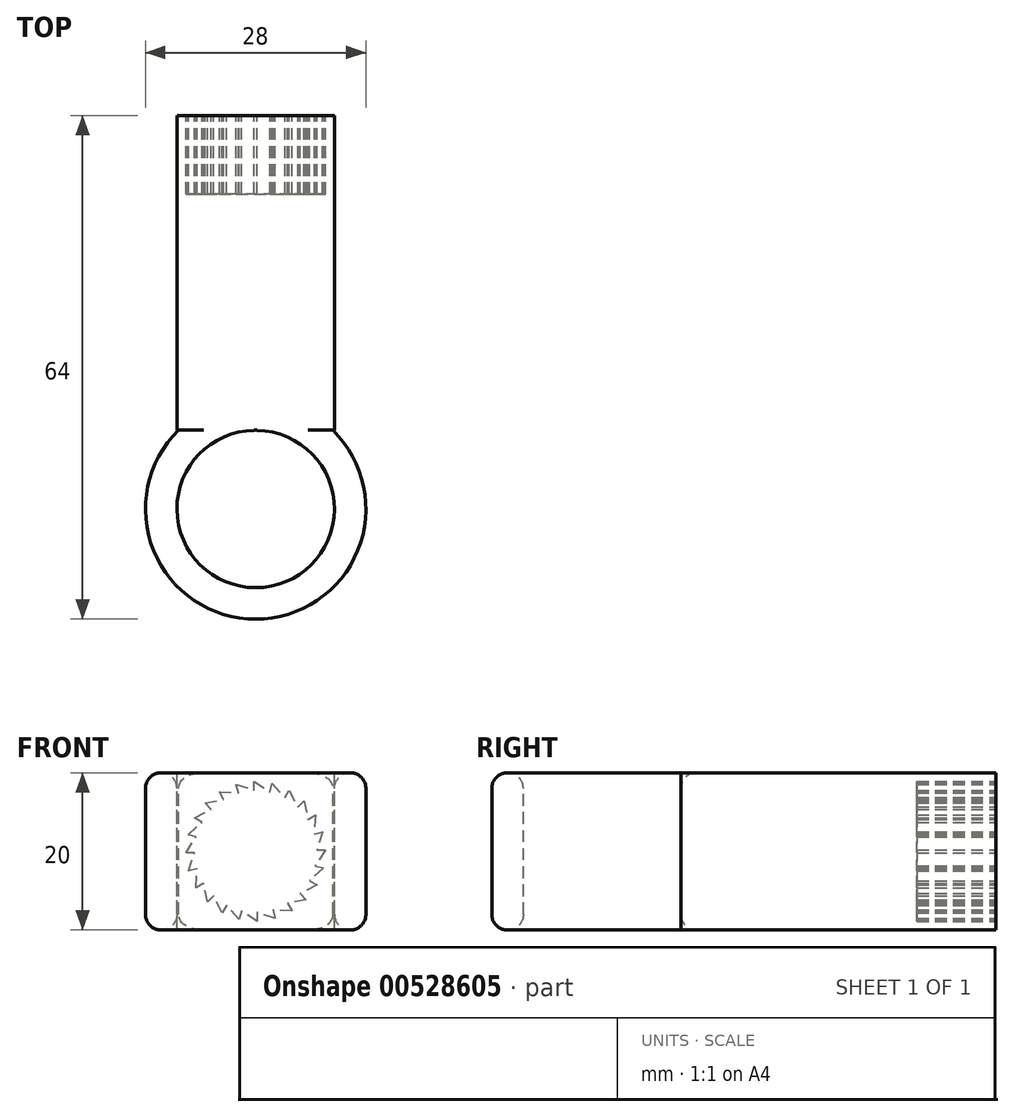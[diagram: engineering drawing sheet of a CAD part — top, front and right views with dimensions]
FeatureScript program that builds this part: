
annotation { "Feature Type Name" : "Feature", "Feature Type Description" : "" }
export const myFeature = defineFeature(function(context is Context, id is Id, definition is map)
    precondition{}
    {
        {
            var Q0;
            Q0=qCreatedBy(makeId("Front.planeOp"),FACE);
            var sketch = newSketch(context, id + "F0", { "sketchPlane" : qUnion([Q0])});
            skLineSegment(sketch, "E0.bottom", {"start": v(0, 0) * mm, "end": v(20, 0) * mm});
            skLineSegment(sketch, "E0.top", {"start": v(0, 20) * mm, "end": v(20, 20) * mm});
            skLineSegment(sketch, "E0.left", {"start": v(0, 0) * mm, "end": v(0, 20) * mm});
            skLineSegment(sketch, "E0.right", {"start": v(20, 0) * mm, "end": v(20, 20) * mm});
            skCircle(sketch, "E1", {"center": v(10, 10) * mm, "radius": 7.5 * mm});
            skLineSegment(sketch, "E2", {"start": v(10, 17.5) * mm, "end": v(10, 18.5) * mm});
            skPoint(sketch, "E3.center", {"position": v(13.24, 8.82) * mm});
            skLineSegment(sketch, "E4", {"start": v(10, 18.5) * mm, "end": v(11.94, 17.24) * mm});
            skLineSegment(sketch, "E5.1.0", {"start": v(12.2, 18.21) * mm, "end": v(13.75, 16.5) * mm});
            skLineSegment(sketch, "E5.1.1", {"start": v(11.94, 17.24) * mm, "end": v(12.2, 18.21) * mm});
            skLineSegment(sketch, "E5.2.0", {"start": v(14.25, 17.36) * mm, "end": v(15.3, 15.3) * mm});
            skLineSegment(sketch, "E5.2.1", {"start": v(13.75, 16.5) * mm, "end": v(14.25, 17.36) * mm});
            skLineSegment(sketch, "E5.3.0", {"start": v(16.01, 16.01) * mm, "end": v(16.5, 13.75) * mm});
            skLineSegment(sketch, "E5.3.1", {"start": v(15.3, 15.3) * mm, "end": v(16.01, 16.01) * mm});
            skLineSegment(sketch, "E5.4.0", {"start": v(17.36, 14.25) * mm, "end": v(17.24, 11.94) * mm});
            skLineSegment(sketch, "E5.4.1", {"start": v(16.5, 13.75) * mm, "end": v(17.36, 14.25) * mm});
            skLineSegment(sketch, "E5.5.0", {"start": v(18.21, 12.2) * mm, "end": v(17.5, 10) * mm});
            skLineSegment(sketch, "E5.5.1", {"start": v(17.24, 11.94) * mm, "end": v(18.21, 12.2) * mm});
            skLineSegment(sketch, "E5.6.0", {"start": v(18.5, 10) * mm, "end": v(17.24, 8.06) * mm});
            skLineSegment(sketch, "E5.6.1", {"start": v(17.5, 10) * mm, "end": v(18.5, 10) * mm});
            skLineSegment(sketch, "E5.7.0", {"start": v(18.21, 7.8) * mm, "end": v(16.5, 6.25) * mm});
            skLineSegment(sketch, "E5.7.1", {"start": v(17.24, 8.06) * mm, "end": v(18.21, 7.8) * mm});
            skLineSegment(sketch, "E5.8.0", {"start": v(17.36, 5.75) * mm, "end": v(15.3, 4.7) * mm});
            skLineSegment(sketch, "E5.8.1", {"start": v(16.5, 6.25) * mm, "end": v(17.36, 5.75) * mm});
            skLineSegment(sketch, "E5.9.0", {"start": v(16.01, 3.99) * mm, "end": v(13.75, 3.5) * mm});
            skLineSegment(sketch, "E5.9.1", {"start": v(15.3, 4.7) * mm, "end": v(16.01, 3.99) * mm});
            skLineSegment(sketch, "E5.10.0", {"start": v(14.25, 2.64) * mm, "end": v(11.94, 2.76) * mm});
            skLineSegment(sketch, "E5.10.1", {"start": v(13.75, 3.5) * mm, "end": v(14.25, 2.64) * mm});
            skLineSegment(sketch, "E5.11.0", {"start": v(12.2, 1.79) * mm, "end": v(10, 2.5) * mm});
            skLineSegment(sketch, "E5.11.1", {"start": v(11.94, 2.76) * mm, "end": v(12.2, 1.79) * mm});
            skLineSegment(sketch, "E5.12.0", {"start": v(10, 1.5) * mm, "end": v(8.06, 2.76) * mm});
            skLineSegment(sketch, "E5.12.1", {"start": v(10, 2.5) * mm, "end": v(10, 1.5) * mm});
            skLineSegment(sketch, "E5.13.0", {"start": v(7.8, 1.79) * mm, "end": v(6.25, 3.5) * mm});
            skLineSegment(sketch, "E5.13.1", {"start": v(8.06, 2.76) * mm, "end": v(7.8, 1.79) * mm});
            skLineSegment(sketch, "E5.14.0", {"start": v(5.75, 2.64) * mm, "end": v(4.7, 4.7) * mm});
            skLineSegment(sketch, "E5.14.1", {"start": v(6.25, 3.5) * mm, "end": v(5.75, 2.64) * mm});
            skLineSegment(sketch, "E5.15.0", {"start": v(3.99, 3.99) * mm, "end": v(3.5, 6.25) * mm});
            skLineSegment(sketch, "E5.15.1", {"start": v(4.7, 4.7) * mm, "end": v(3.99, 3.99) * mm});
            skLineSegment(sketch, "E5.16.0", {"start": v(2.64, 5.75) * mm, "end": v(2.76, 8.06) * mm});
            skLineSegment(sketch, "E5.16.1", {"start": v(3.5, 6.25) * mm, "end": v(2.64, 5.75) * mm});
            skLineSegment(sketch, "E5.17.0", {"start": v(1.79, 7.8) * mm, "end": v(2.5, 10) * mm});
            skLineSegment(sketch, "E5.17.1", {"start": v(2.76, 8.06) * mm, "end": v(1.79, 7.8) * mm});
            skLineSegment(sketch, "E5.18.0", {"start": v(1.5, 10) * mm, "end": v(2.76, 11.94) * mm});
            skLineSegment(sketch, "E5.18.1", {"start": v(2.5, 10) * mm, "end": v(1.5, 10) * mm});
            skLineSegment(sketch, "E5.19.0", {"start": v(1.79, 12.2) * mm, "end": v(3.5, 13.75) * mm});
            skLineSegment(sketch, "E5.19.1", {"start": v(2.76, 11.94) * mm, "end": v(1.79, 12.2) * mm});
            skLineSegment(sketch, "E5.20.0", {"start": v(2.64, 14.25) * mm, "end": v(4.7, 15.3) * mm});
            skLineSegment(sketch, "E5.20.1", {"start": v(3.5, 13.75) * mm, "end": v(2.64, 14.25) * mm});
            skLineSegment(sketch, "E5.21.0", {"start": v(3.99, 16.01) * mm, "end": v(6.25, 16.5) * mm});
            skLineSegment(sketch, "E5.21.1", {"start": v(4.7, 15.3) * mm, "end": v(3.99, 16.01) * mm});
            skLineSegment(sketch, "E5.22.0", {"start": v(5.75, 17.36) * mm, "end": v(8.06, 17.24) * mm});
            skLineSegment(sketch, "E5.22.1", {"start": v(6.25, 16.5) * mm, "end": v(5.75, 17.36) * mm});
            skLineSegment(sketch, "E5.anchor1", {"start": v(10, 10) * mm, "end": v(10, 17.5) * mm, "construction": true});
            skLineSegment(sketch, "E5.anchor2", {"start": v(10, 10) * mm, "end": v(8.06, 17.24) * mm, "construction": true});
            skLineSegment(sketch, "E6.3.23.0", {"start": v(8.06, 17.24) * mm, "end": v(7.8, 18.21) * mm});
            skLineSegment(sketch, "E6.4.23.0", {"start": v(7.8, 18.21) * mm, "end": v(10, 17.5) * mm});
            skLineSegment(sketch, "E7.0", {"start": v(18.51, 12.49) * mm, "end": v(17.77, 10.2) * mm});
            skLineSegment(sketch, "E7.1", {"start": v(17.46, 12.2) * mm, "end": v(18.51, 12.49) * mm});
            skLineSegment(sketch, "E7.2", {"start": v(2.42, 5.4) * mm, "end": v(2.54, 7.8) * mm});
            skLineSegment(sketch, "E7.3", {"start": v(3.37, 5.94) * mm, "end": v(2.42, 5.4) * mm});
            skLineSegment(sketch, "E7.4", {"start": v(3.87, 3.59) * mm, "end": v(3.37, 5.94) * mm});
            skLineSegment(sketch, "E7.5", {"start": v(4.64, 4.36) * mm, "end": v(3.87, 3.59) * mm});
            skLineSegment(sketch, "E7.6", {"start": v(5.74, 2.22) * mm, "end": v(4.64, 4.36) * mm});
            skLineSegment(sketch, "E7.7", {"start": v(6.29, 3.17) * mm, "end": v(5.74, 2.22) * mm});
            skLineSegment(sketch, "E7.8", {"start": v(7.9, 1.38) * mm, "end": v(6.29, 3.17) * mm});
            skLineSegment(sketch, "E7.9", {"start": v(8.18, 2.44) * mm, "end": v(7.9, 1.38) * mm});
            skLineSegment(sketch, "E7.10", {"start": v(10.2, 1.13) * mm, "end": v(8.18, 2.44) * mm});
            skLineSegment(sketch, "E7.11", {"start": v(10.2, 2.23) * mm, "end": v(10.2, 1.13) * mm});
            skLineSegment(sketch, "E7.12", {"start": v(12.49, 1.49) * mm, "end": v(10.2, 2.23) * mm});
            skLineSegment(sketch, "E7.13", {"start": v(12.2, 2.54) * mm, "end": v(12.49, 1.49) * mm});
            skLineSegment(sketch, "E7.14", {"start": v(18.62, 7.9) * mm, "end": v(16.83, 6.29) * mm});
            skLineSegment(sketch, "E7.15", {"start": v(17.56, 8.18) * mm, "end": v(18.62, 7.9) * mm});
            skLineSegment(sketch, "E7.16", {"start": v(18.87, 10.2) * mm, "end": v(17.56, 8.18) * mm});
            skLineSegment(sketch, "E7.17", {"start": v(17.77, 10.2) * mm, "end": v(18.87, 10.2) * mm});
            skLineSegment(sketch, "E7.18", {"start": v(16.83, 6.29) * mm, "end": v(17.78, 5.74) * mm});
            skLineSegment(sketch, "E7.19", {"start": v(17.78, 5.74) * mm, "end": v(15.64, 4.64) * mm});
            skLineSegment(sketch, "E7.20", {"start": v(15.64, 4.64) * mm, "end": v(16.41, 3.87) * mm});
            skLineSegment(sketch, "E7.21", {"start": v(16.41, 3.87) * mm, "end": v(14.06, 3.37) * mm});
            skLineSegment(sketch, "E7.22", {"start": v(14.06, 3.37) * mm, "end": v(14.6, 2.42) * mm});
            skLineSegment(sketch, "E7.23", {"start": v(14.6, 2.42) * mm, "end": v(12.2, 2.54) * mm});
            skLineSegment(sketch, "E7.24", {"start": v(2.54, 7.8) * mm, "end": v(1.49, 7.51) * mm});
            skLineSegment(sketch, "E7.25", {"start": v(1.49, 7.51) * mm, "end": v(2.23, 9.8) * mm});
            skLineSegment(sketch, "E7.26", {"start": v(2.23, 9.8) * mm, "end": v(1.13, 9.8) * mm});
            skLineSegment(sketch, "E7.27", {"start": v(1.13, 9.8) * mm, "end": v(2.44, 11.82) * mm});
            skLineSegment(sketch, "E7.28", {"start": v(2.44, 11.82) * mm, "end": v(1.38, 12.1) * mm});
            skLineSegment(sketch, "E7.29", {"start": v(1.38, 12.1) * mm, "end": v(3.17, 13.71) * mm});
            skLineSegment(sketch, "E7.30", {"start": v(3.17, 13.71) * mm, "end": v(2.22, 14.26) * mm});
            skLineSegment(sketch, "E7.31", {"start": v(2.22, 14.26) * mm, "end": v(4.36, 15.36) * mm});
            skLineSegment(sketch, "E7.32", {"start": v(4.36, 15.36) * mm, "end": v(3.59, 16.13) * mm});
            skLineSegment(sketch, "E7.33", {"start": v(3.59, 16.13) * mm, "end": v(5.94, 16.63) * mm});
            skLineSegment(sketch, "E7.34", {"start": v(5.94, 16.63) * mm, "end": v(5.4, 17.58) * mm});
            skLineSegment(sketch, "E7.35", {"start": v(5.4, 17.58) * mm, "end": v(7.8, 17.46) * mm});
            skLineSegment(sketch, "E7.36", {"start": v(7.8, 17.46) * mm, "end": v(7.51, 18.51) * mm});
            skLineSegment(sketch, "E7.37", {"start": v(7.51, 18.51) * mm, "end": v(9.8, 17.77) * mm});
            skLineSegment(sketch, "E7.38", {"start": v(9.8, 17.77) * mm, "end": v(9.8, 18.87) * mm});
            skLineSegment(sketch, "E7.39", {"start": v(9.8, 18.87) * mm, "end": v(11.82, 17.56) * mm});
            skLineSegment(sketch, "E7.40", {"start": v(11.82, 17.56) * mm, "end": v(12.1, 18.62) * mm});
            skLineSegment(sketch, "E7.41", {"start": v(12.1, 18.62) * mm, "end": v(13.71, 16.83) * mm});
            skLineSegment(sketch, "E7.42", {"start": v(13.71, 16.83) * mm, "end": v(14.26, 17.78) * mm});
            skLineSegment(sketch, "E7.43", {"start": v(14.26, 17.78) * mm, "end": v(15.36, 15.64) * mm});
            skLineSegment(sketch, "E7.44", {"start": v(15.36, 15.64) * mm, "end": v(16.13, 16.41) * mm});
            skLineSegment(sketch, "E7.45", {"start": v(16.13, 16.41) * mm, "end": v(16.63, 14.06) * mm});
            skLineSegment(sketch, "E7.46", {"start": v(16.63, 14.06) * mm, "end": v(17.58, 14.6) * mm});
            skLineSegment(sketch, "E7.47", {"start": v(17.58, 14.6) * mm, "end": v(17.46, 12.2) * mm});
            skSolve(sketch);
        }
        {
            var Q0;
            Q0 = qSketchRegion(id + "F0", true);
            var Q1;
            {var subQ0=sQuery(id+"F0.wireOp",EDGE,"E1");var subQ17=makeQuery(id+"F0.imprint","INTERSECT",VERTEX,{"derivedFrom":[subQ0,sQuery(id+"F0.wireOp",EDGE,"E5.4.0"),sQuery(id+"F0.wireOp",EDGE,"E5.5.1")]});Q1=makeQuery(id+"F0.imprint","IMPRINT",FACE,{"disambiguationData":[TD([[makeQuery(id+"F0.imprint","IMPRINT",EDGE,{"disambiguationData":[TD([[subQ17,1.0]])],"derivedFrom":subQ0}),1.0]])]});}
            var Q2;
            {var subQ2=sQuery(id+"F0.wireOp",EDGE,"E5.19.0");Q2=makeQuery(id+"F0.imprint","IMPRINT",FACE,{"disambiguationData":[TD([[makeQuery(id+"F0.imprint","IMPRINT",EDGE,{"derivedFrom":subQ2}),-1.0]])]});}
            var Q3;
            {var subQ2=sQuery(id+"F0.wireOp",EDGE,"E5.20.0");Q3=makeQuery(id+"F0.imprint","IMPRINT",FACE,{"disambiguationData":[TD([[makeQuery(id+"F0.imprint","IMPRINT",EDGE,{"derivedFrom":subQ2}),-1.0]])]});}
            var Q4;
            {var subQ2=sQuery(id+"F0.wireOp",EDGE,"E5.21.0");Q4=makeQuery(id+"F0.imprint","IMPRINT",FACE,{"disambiguationData":[TD([[makeQuery(id+"F0.imprint","IMPRINT",EDGE,{"derivedFrom":subQ2}),-1.0]])]});}
            var Q5;
            Q5=makeQuery(id+"F0.imprint","IMPRINT",FACE,{"disambiguationData":[TD([[makeQuery(id+"F0.imprint","IMPRINT",EDGE,{"derivedFrom":sQuery(id+"F0.wireOp",EDGE,"E2")}),1.0]])]});
            var Q6;
            {var subQ2=sQuery(id+"F0.wireOp",EDGE,"E5.22.0");Q6=makeQuery(id+"F0.imprint","IMPRINT",FACE,{"disambiguationData":[TD([[makeQuery(id+"F0.imprint","IMPRINT",EDGE,{"derivedFrom":subQ2}),-1.0]])]});}
            var Q7;
            {var subQ2=sQuery(id+"F0.wireOp",EDGE,"E6.3.23.0");Q7=makeQuery(id+"F0.imprint","IMPRINT",FACE,{"disambiguationData":[TD([[makeQuery(id+"F0.imprint","IMPRINT",EDGE,{"derivedFrom":subQ2}),-1.0]])]});}
            var Q8;
            {var subQ0=sQuery(id+"F0.wireOp",EDGE,"E2");Q8=makeQuery(id+"F0.imprint","IMPRINT",FACE,{"disambiguationData":[TD([[makeQuery(id+"F0.imprint","IMPRINT",EDGE,{"derivedFrom":subQ0}),-1.0]])]});}
            var Q9;
            {var subQ2=sQuery(id+"F0.wireOp",EDGE,"E5.1.0");Q9=makeQuery(id+"F0.imprint","IMPRINT",FACE,{"disambiguationData":[TD([[makeQuery(id+"F0.imprint","IMPRINT",EDGE,{"derivedFrom":subQ2}),-1.0]])]});}
            var Q10;
            {var subQ2=sQuery(id+"F0.wireOp",EDGE,"E5.2.0");Q10=makeQuery(id+"F0.imprint","IMPRINT",FACE,{"disambiguationData":[TD([[makeQuery(id+"F0.imprint","IMPRINT",EDGE,{"derivedFrom":subQ2}),-1.0]])]});}
            var Q11;
            {var subQ2=sQuery(id+"F0.wireOp",EDGE,"E5.3.0");Q11=makeQuery(id+"F0.imprint","IMPRINT",FACE,{"disambiguationData":[TD([[makeQuery(id+"F0.imprint","IMPRINT",EDGE,{"derivedFrom":subQ2}),-1.0]])]});}
            var Q12;
            {var subQ2=sQuery(id+"F0.wireOp",EDGE,"E5.4.0");Q12=makeQuery(id+"F0.imprint","IMPRINT",FACE,{"disambiguationData":[TD([[makeQuery(id+"F0.imprint","IMPRINT",EDGE,{"derivedFrom":subQ2}),-1.0]])]});}
            var Q13;
            {var subQ2=sQuery(id+"F0.wireOp",EDGE,"E5.5.0");Q13=makeQuery(id+"F0.imprint","IMPRINT",FACE,{"disambiguationData":[TD([[makeQuery(id+"F0.imprint","IMPRINT",EDGE,{"derivedFrom":subQ2}),-1.0]])]});}
            var Q14;
            {var subQ2=sQuery(id+"F0.wireOp",EDGE,"E5.6.0");Q14=makeQuery(id+"F0.imprint","IMPRINT",FACE,{"disambiguationData":[TD([[makeQuery(id+"F0.imprint","IMPRINT",EDGE,{"derivedFrom":subQ2}),-1.0]])]});}
            var Q15;
            {var subQ2=sQuery(id+"F0.wireOp",EDGE,"E5.7.0");Q15=makeQuery(id+"F0.imprint","IMPRINT",FACE,{"disambiguationData":[TD([[makeQuery(id+"F0.imprint","IMPRINT",EDGE,{"derivedFrom":subQ2}),-1.0]])]});}
            var Q16;
            {var subQ2=sQuery(id+"F0.wireOp",EDGE,"E5.8.0");Q16=makeQuery(id+"F0.imprint","IMPRINT",FACE,{"disambiguationData":[TD([[makeQuery(id+"F0.imprint","IMPRINT",EDGE,{"derivedFrom":subQ2}),-1.0]])]});}
            var Q17;
            {var subQ2=sQuery(id+"F0.wireOp",EDGE,"E5.9.0");Q17=makeQuery(id+"F0.imprint","IMPRINT",FACE,{"disambiguationData":[TD([[makeQuery(id+"F0.imprint","IMPRINT",EDGE,{"derivedFrom":subQ2}),-1.0]])]});}
            var Q18;
            {var subQ2=sQuery(id+"F0.wireOp",EDGE,"E5.10.0");Q18=makeQuery(id+"F0.imprint","IMPRINT",FACE,{"disambiguationData":[TD([[makeQuery(id+"F0.imprint","IMPRINT",EDGE,{"derivedFrom":subQ2}),-1.0]])]});}
            var Q19;
            {var subQ2=sQuery(id+"F0.wireOp",EDGE,"E5.11.0");Q19=makeQuery(id+"F0.imprint","IMPRINT",FACE,{"disambiguationData":[TD([[makeQuery(id+"F0.imprint","IMPRINT",EDGE,{"derivedFrom":subQ2}),-1.0]])]});}
            var Q20;
            {var subQ2=sQuery(id+"F0.wireOp",EDGE,"E5.12.0");Q20=makeQuery(id+"F0.imprint","IMPRINT",FACE,{"disambiguationData":[TD([[makeQuery(id+"F0.imprint","IMPRINT",EDGE,{"derivedFrom":subQ2}),-1.0]])]});}
            var Q21;
            {var subQ2=sQuery(id+"F0.wireOp",EDGE,"E5.13.0");Q21=makeQuery(id+"F0.imprint","IMPRINT",FACE,{"disambiguationData":[TD([[makeQuery(id+"F0.imprint","IMPRINT",EDGE,{"derivedFrom":subQ2}),-1.0]])]});}
            var Q22;
            {var subQ2=sQuery(id+"F0.wireOp",EDGE,"E5.14.0");Q22=makeQuery(id+"F0.imprint","IMPRINT",FACE,{"disambiguationData":[TD([[makeQuery(id+"F0.imprint","IMPRINT",EDGE,{"derivedFrom":subQ2}),-1.0]])]});}
            var Q23;
            {var subQ2=sQuery(id+"F0.wireOp",EDGE,"E5.15.0");Q23=makeQuery(id+"F0.imprint","IMPRINT",FACE,{"disambiguationData":[TD([[makeQuery(id+"F0.imprint","IMPRINT",EDGE,{"derivedFrom":subQ2}),-1.0]])]});}
            var Q24;
            {var subQ2=sQuery(id+"F0.wireOp",EDGE,"E5.16.0");Q24=makeQuery(id+"F0.imprint","IMPRINT",FACE,{"disambiguationData":[TD([[makeQuery(id+"F0.imprint","IMPRINT",EDGE,{"derivedFrom":subQ2}),-1.0]])]});}
            var Q25;
            {var subQ2=sQuery(id+"F0.wireOp",EDGE,"E5.17.0");Q25=makeQuery(id+"F0.imprint","IMPRINT",FACE,{"disambiguationData":[TD([[makeQuery(id+"F0.imprint","IMPRINT",EDGE,{"derivedFrom":subQ2}),-1.0]])]});}
            var Q26;
            {var subQ2=sQuery(id+"F0.wireOp",EDGE,"E5.18.0");Q26=makeQuery(id+"F0.imprint","IMPRINT",FACE,{"disambiguationData":[TD([[makeQuery(id+"F0.imprint","IMPRINT",EDGE,{"derivedFrom":subQ2}),-1.0]])]});}
            extrude(context, id + "F1", {"entities" : qUnion([Q0, Q1, Q2, Q3, Q4, Q5, Q6, Q7, Q8, Q9, Q10, Q11, Q12, Q13, Q14, Q15, Q16, Q17, Q18, Q19, Q20, Q21, Q22, Q23, Q24, Q25, Q26]), "depth" : 40 * mm, "offsetDistance" : 25 * mm});
        }
        {
            var Q0;
            {var subQ0=sQuery(id+"F0.wireOp",EDGE,"E1");var subQ17=makeQuery(id+"F0.imprint","INTERSECT",VERTEX,{"derivedFrom":[subQ0,sQuery(id+"F0.wireOp",EDGE,"E5.4.0"),sQuery(id+"F0.wireOp",EDGE,"E5.5.1")]});Q0=makeQuery(id+"F0.imprint","IMPRINT",FACE,{"disambiguationData":[TD([[makeQuery(id+"F0.imprint","IMPRINT",EDGE,{"disambiguationData":[TD([[subQ17,1.0]])],"derivedFrom":subQ0}),1.0]])]});}
            var Q1;
            {var subQ2=sQuery(id+"F0.wireOp",EDGE,"E5.3.0");Q1=makeQuery(id+"F0.imprint","IMPRINT",FACE,{"disambiguationData":[TD([[makeQuery(id+"F0.imprint","IMPRINT",EDGE,{"derivedFrom":subQ2}),-1.0]])]});}
            var Q2;
            {var subQ2=sQuery(id+"F0.wireOp",EDGE,"E5.2.0");Q2=makeQuery(id+"F0.imprint","IMPRINT",FACE,{"disambiguationData":[TD([[makeQuery(id+"F0.imprint","IMPRINT",EDGE,{"derivedFrom":subQ2}),-1.0]])]});}
            var Q3;
            {var subQ2=sQuery(id+"F0.wireOp",EDGE,"E5.1.0");Q3=makeQuery(id+"F0.imprint","IMPRINT",FACE,{"disambiguationData":[TD([[makeQuery(id+"F0.imprint","IMPRINT",EDGE,{"derivedFrom":subQ2}),-1.0]])]});}
            var Q4;
            {var subQ0=sQuery(id+"F0.wireOp",EDGE,"E2");Q4=makeQuery(id+"F0.imprint","IMPRINT",FACE,{"disambiguationData":[TD([[makeQuery(id+"F0.imprint","IMPRINT",EDGE,{"derivedFrom":subQ0}),-1.0]])]});}
            var Q5;
            {var subQ2=sQuery(id+"F0.wireOp",EDGE,"E6.3.23.0");Q5=makeQuery(id+"F0.imprint","IMPRINT",FACE,{"disambiguationData":[TD([[makeQuery(id+"F0.imprint","IMPRINT",EDGE,{"derivedFrom":subQ2}),-1.0]])]});}
            var Q6;
            {var subQ2=sQuery(id+"F0.wireOp",EDGE,"E5.22.0");Q6=makeQuery(id+"F0.imprint","IMPRINT",FACE,{"disambiguationData":[TD([[makeQuery(id+"F0.imprint","IMPRINT",EDGE,{"derivedFrom":subQ2}),-1.0]])]});}
            var Q7;
            {var subQ2=sQuery(id+"F0.wireOp",EDGE,"E5.21.0");Q7=makeQuery(id+"F0.imprint","IMPRINT",FACE,{"disambiguationData":[TD([[makeQuery(id+"F0.imprint","IMPRINT",EDGE,{"derivedFrom":subQ2}),-1.0]])]});}
            var Q8;
            {var subQ2=sQuery(id+"F0.wireOp",EDGE,"E5.20.0");Q8=makeQuery(id+"F0.imprint","IMPRINT",FACE,{"disambiguationData":[TD([[makeQuery(id+"F0.imprint","IMPRINT",EDGE,{"derivedFrom":subQ2}),-1.0]])]});}
            var Q9;
            {var subQ2=sQuery(id+"F0.wireOp",EDGE,"E5.19.0");Q9=makeQuery(id+"F0.imprint","IMPRINT",FACE,{"disambiguationData":[TD([[makeQuery(id+"F0.imprint","IMPRINT",EDGE,{"derivedFrom":subQ2}),-1.0]])]});}
            var Q10;
            {var subQ2=sQuery(id+"F0.wireOp",EDGE,"E5.18.0");Q10=makeQuery(id+"F0.imprint","IMPRINT",FACE,{"disambiguationData":[TD([[makeQuery(id+"F0.imprint","IMPRINT",EDGE,{"derivedFrom":subQ2}),-1.0]])]});}
            var Q11;
            {var subQ2=sQuery(id+"F0.wireOp",EDGE,"E5.17.0");Q11=makeQuery(id+"F0.imprint","IMPRINT",FACE,{"disambiguationData":[TD([[makeQuery(id+"F0.imprint","IMPRINT",EDGE,{"derivedFrom":subQ2}),-1.0]])]});}
            var Q12;
            {var subQ2=sQuery(id+"F0.wireOp",EDGE,"E5.16.0");Q12=makeQuery(id+"F0.imprint","IMPRINT",FACE,{"disambiguationData":[TD([[makeQuery(id+"F0.imprint","IMPRINT",EDGE,{"derivedFrom":subQ2}),-1.0]])]});}
            var Q13;
            {var subQ2=sQuery(id+"F0.wireOp",EDGE,"E5.15.0");Q13=makeQuery(id+"F0.imprint","IMPRINT",FACE,{"disambiguationData":[TD([[makeQuery(id+"F0.imprint","IMPRINT",EDGE,{"derivedFrom":subQ2}),-1.0]])]});}
            var Q14;
            {var subQ2=sQuery(id+"F0.wireOp",EDGE,"E5.14.0");Q14=makeQuery(id+"F0.imprint","IMPRINT",FACE,{"disambiguationData":[TD([[makeQuery(id+"F0.imprint","IMPRINT",EDGE,{"derivedFrom":subQ2}),-1.0]])]});}
            var Q15;
            {var subQ2=sQuery(id+"F0.wireOp",EDGE,"E5.13.0");Q15=makeQuery(id+"F0.imprint","IMPRINT",FACE,{"disambiguationData":[TD([[makeQuery(id+"F0.imprint","IMPRINT",EDGE,{"derivedFrom":subQ2}),-1.0]])]});}
            var Q16;
            {var subQ2=sQuery(id+"F0.wireOp",EDGE,"E5.12.0");Q16=makeQuery(id+"F0.imprint","IMPRINT",FACE,{"disambiguationData":[TD([[makeQuery(id+"F0.imprint","IMPRINT",EDGE,{"derivedFrom":subQ2}),-1.0]])]});}
            var Q17;
            {var subQ2=sQuery(id+"F0.wireOp",EDGE,"E5.11.0");Q17=makeQuery(id+"F0.imprint","IMPRINT",FACE,{"disambiguationData":[TD([[makeQuery(id+"F0.imprint","IMPRINT",EDGE,{"derivedFrom":subQ2}),-1.0]])]});}
            var Q18;
            {var subQ2=sQuery(id+"F0.wireOp",EDGE,"E5.10.0");Q18=makeQuery(id+"F0.imprint","IMPRINT",FACE,{"disambiguationData":[TD([[makeQuery(id+"F0.imprint","IMPRINT",EDGE,{"derivedFrom":subQ2}),-1.0]])]});}
            var Q19;
            {var subQ2=sQuery(id+"F0.wireOp",EDGE,"E5.9.0");Q19=makeQuery(id+"F0.imprint","IMPRINT",FACE,{"disambiguationData":[TD([[makeQuery(id+"F0.imprint","IMPRINT",EDGE,{"derivedFrom":subQ2}),-1.0]])]});}
            var Q20;
            {var subQ2=sQuery(id+"F0.wireOp",EDGE,"E5.6.0");Q20=makeQuery(id+"F0.imprint","IMPRINT",FACE,{"disambiguationData":[TD([[makeQuery(id+"F0.imprint","IMPRINT",EDGE,{"derivedFrom":subQ2}),-1.0]])]});}
            var Q21;
            {var subQ2=sQuery(id+"F0.wireOp",EDGE,"E5.7.0");Q21=makeQuery(id+"F0.imprint","IMPRINT",FACE,{"disambiguationData":[TD([[makeQuery(id+"F0.imprint","IMPRINT",EDGE,{"derivedFrom":subQ2}),-1.0]])]});}
            var Q22;
            {var subQ2=sQuery(id+"F0.wireOp",EDGE,"E5.8.0");Q22=makeQuery(id+"F0.imprint","IMPRINT",FACE,{"disambiguationData":[TD([[makeQuery(id+"F0.imprint","IMPRINT",EDGE,{"derivedFrom":subQ2}),-1.0]])]});}
            var Q23;
            {var subQ2=sQuery(id+"F0.wireOp",EDGE,"E5.5.0");Q23=makeQuery(id+"F0.imprint","IMPRINT",FACE,{"disambiguationData":[TD([[makeQuery(id+"F0.imprint","IMPRINT",EDGE,{"derivedFrom":subQ2}),-1.0]])]});}
            var Q24;
            {var subQ2=sQuery(id+"F0.wireOp",EDGE,"E5.4.0");Q24=makeQuery(id+"F0.imprint","IMPRINT",FACE,{"disambiguationData":[TD([[makeQuery(id+"F0.imprint","IMPRINT",EDGE,{"derivedFrom":subQ2}),-1.0]])]});}
            var Q25;
            Q25=makeQuery(id+"F0.imprint","IMPRINT",FACE,{"disambiguationData":[TD([[makeQuery(id+"F0.imprint","IMPRINT",EDGE,{"derivedFrom":sQuery(id+"F0.wireOp",EDGE,"E2")}),1.0]])]});
            extrude(context, id + "F2", {"entities" : qUnion([Q0, Q1, Q2, Q3, Q4, Q5, Q6, Q7, Q8, Q9, Q10, Q11, Q12, Q13, Q14, Q15, Q16, Q17, Q18, Q19, Q20, Q21, Q22, Q23, Q24, Q25]), "operationType" : NewBodyOperationType.REMOVE, "depth" : 10 * mm, "offsetDistance" : 25 * mm});
        }
        {
            var Q0;
            Q0=makeQuery(id+"F1.opExtrude","SWEPT_FACE",FACE,{"disambiguationData":[OSD([sQuery(id+"F0.wireOp",EDGE,"E0.top")])]});
            var sketch = newSketch(context, id + "F3", { "sketchPlane" : qUnion([Q0])});
            skCircle(sketch, "E8", {"center": v(10, -50) * mm, "radius": 10 * mm});
            skPoint(sketch, "E8.first.point", {"position": v(0, -50) * mm});
            skPoint(sketch, "E8.second.point", {"position": v(20, -50) * mm});
            skPoint(sketch, "E8.third.point", {"position": v(10.16, -60) * mm});
            skCircle(sketch, "E9.0", {"center": v(10, -50) * mm, "radius": 14 * mm});
            skSolve(sketch);
        }
        {
            var Q0;
            {var subQ0=sQuery(id+"F3.wireOp",EDGE,"E8");var subQ1=makeQuery(id+"F1.opExtrude","CAP_EDGE",EDGE,{"disambiguationData":[OSD([sQuery(id+"F0.wireOp",EDGE,"E0.top")])],"isStart":false});var subQ2=makeQuery(id+"F3.imprint","INTERSECT",VERTEX,{"disambiguationData":[OD(0.0)],"derivedFrom":[subQ1,subQ0]});Q0=makeQuery(id+"F3.imprint","IMPRINT",FACE,{"disambiguationData":[TD([[makeQuery(id+"F3.imprint","IMPRINT",EDGE,{"disambiguationData":[TD([[subQ2,-1.0]])],"derivedFrom":subQ0}),-1.0]])]});}
            extrude(context, id + "F4", {"entities" : qUnion([Q0]), "operationType" : NewBodyOperationType.ADD, "oppositeDirection" : true, "depth" : 20 * mm, "offsetDistance" : 25 * mm});
        }
        {
            var Q0;
            Q0=makeQuery(id+"F4.opExtrude","CAP_EDGE",EDGE,{"disambiguationData":[OSD([sQuery(id+"F3.wireOp",EDGE,"E8")])],"isStart":true});
            var Q1;
            Q1=makeQuery(id+"F4.opExtrude","CAP_EDGE",EDGE,{"disambiguationData":[OSD([sQuery(id+"F3.wireOp",EDGE,"E9.0")])],"isStart":true});
            var Q2;
            Q2=makeQuery(id+"F4.opExtrude","CAP_EDGE",EDGE,{"disambiguationData":[OSD([sQuery(id+"F3.wireOp",EDGE,"E9.0")])],"isStart":false});
            var Q3;
            Q3=makeQuery(id+"F4.opExtrude","CAP_EDGE",EDGE,{"disambiguationData":[OSD([sQuery(id+"F3.wireOp",EDGE,"E8")])],"isStart":false});
            var Q4;
            {var subQ1=sQuery(id+"F3.wireOp",EDGE,"E8");var subQ2=sQuery(id+"F0.wireOp",EDGE,"E0.top");var subQ3=sQuery(id+"F0.wireOp",EDGE,"E0.bottom");Q4=makeQuery(id+"F4.boolean.opBoolean","SPLIT",FACE,{"disambiguationData":[TD([makeQuery(id+"F4.opExtrude","SWEPT_FACE",FACE,{"disambiguationData":[OSD([subQ1])]})])],"derivedFrom":makeQuery(id+"F1.opExtrude","CAP_FACE",FACE,{"disambiguationData":[OSD([subQ3,subQ2,sQuery(id+"F0.wireOp",EDGE,"E0.left"),sQuery(id+"F0.wireOp",EDGE,"E0.right")])],"isStart":false})});}
            fillet(context, id + "F5", {"entities" : qUnion([Q0, Q1, Q2, Q3, Q4]), "radius" : 2 * mm, "tangentPropagation" : true, "allowEdgeOverflow" : false});
        }
    });
